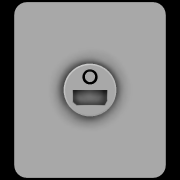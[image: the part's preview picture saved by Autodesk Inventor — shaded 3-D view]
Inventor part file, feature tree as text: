
AUTODESK INVENTOR PART (.ipt)
format: ipt  version: 2020 (Build 240168000, 168)  size: 158,720 bytes
history: native  units: in
note: dims shown in document units (in); Inventor stores cm internally (conversion verified against a paired STEP export)
features: extrude x3, other x2, chamfer x1, fillet x1
ambient origin geometry x8: Origin, YZ Plane, XZ Plane, XY Plane, X Axis, Y Axis, Z Axis, Center Point
bodies: Body1 (feature_tree)
feature tree (7):
  other  "FishmanBattery"
  extrude  "FishmanBatteryFeature"  Depth=1.5in
  extrude  "FishmanBatteryConnectorFeature"  Depth=1.74in
  chamfer  "FishmanBatteryChamferFeature"  Distance=0.5in
  fillet  "FishmanBatteryFilletsFeature"  Radius=0.4in
  extrude  "FishmanConnectorHolesFeature"  Depth=0.15in TaperAngle=0.0deg
  other  "FishmanConnector"
